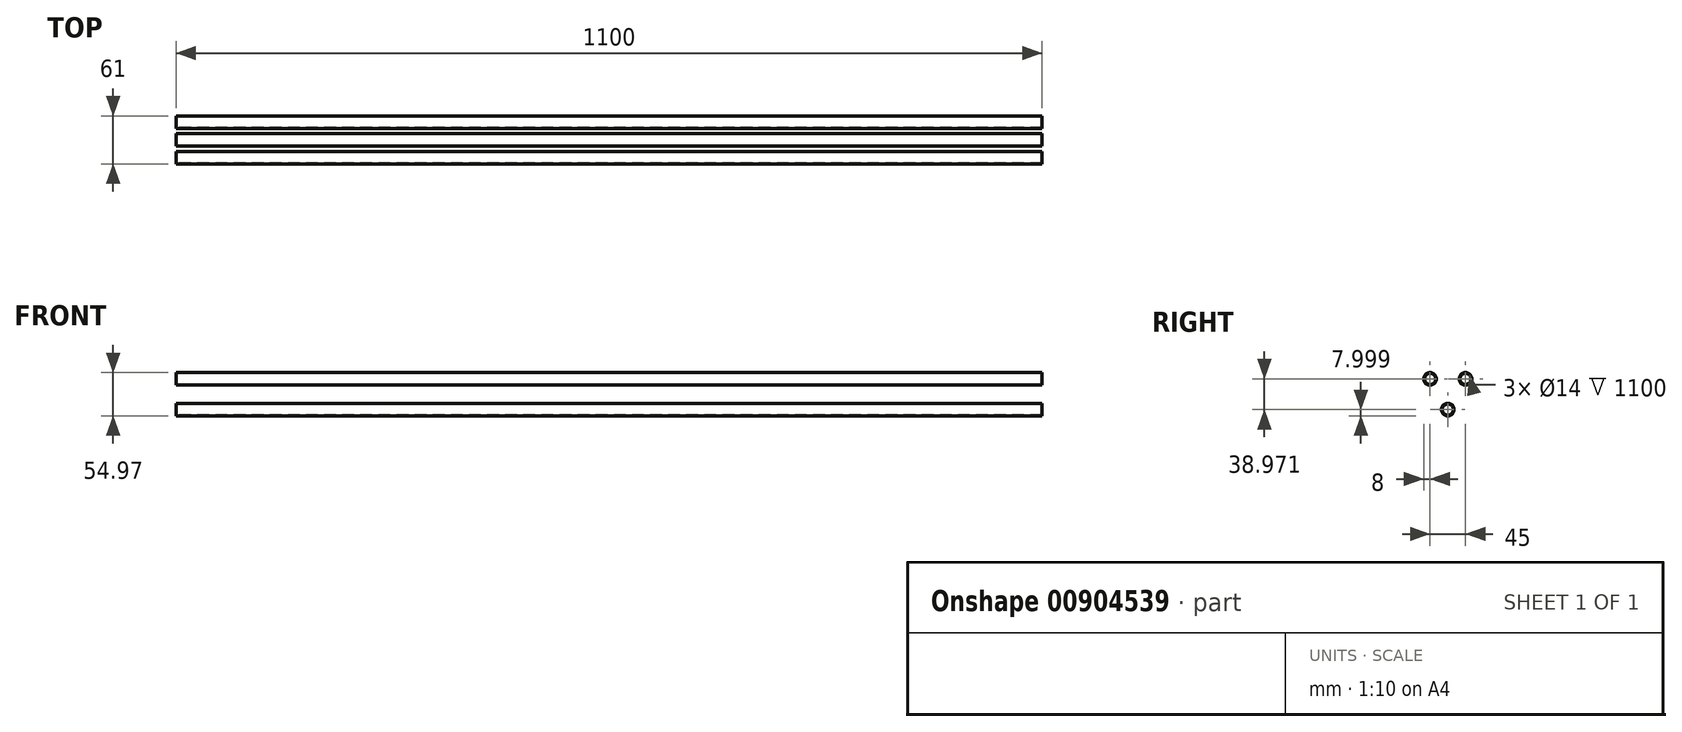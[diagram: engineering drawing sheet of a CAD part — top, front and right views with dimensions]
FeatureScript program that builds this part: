
annotation { "Feature Type Name" : "Feature", "Feature Type Description" : "" }
export const myFeature = defineFeature(function(context is Context, id is Id, definition is map)
    precondition{}
    {
        {
            var Q0;
            Q0=qCreatedBy(makeId("Right.planeOp"),FACE);
            var sketch = newSketch(context, id + "F0", { "sketchPlane" : qUnion([Q0])});
            skCircle(sketch, "E0", {"center": v(0, 0) * mm, "radius": 8 * mm});
            skCircle(sketch, "E1", {"center": v(45, 0) * mm, "radius": 8 * mm});
            skCircle(sketch, "E2", {"center": v(22.5, -38.97) * mm, "radius": 8 * mm});
            skCircle(sketch, "E3", {"center": v(0, 0) * mm, "radius": 7 * mm});
            skCircle(sketch, "E4", {"center": v(45, 0) * mm, "radius": 7 * mm});
            skCircle(sketch, "E5", {"center": v(22.5, -38.97) * mm, "radius": 7 * mm});
            skSolve(sketch);
        }
        {
            var Q0;
            Q0=makeQuery(id+"F0.imprint","IMPRINT",FACE,{"disambiguationData":[TD([[makeQuery(id+"F0.imprint","IMPRINT",EDGE,{"derivedFrom":sQuery(id+"F0.wireOp",EDGE,"E0")}),1.0]])]});
            var Q1;
            Q1=makeQuery(id+"F0.imprint","IMPRINT",FACE,{"disambiguationData":[TD([[makeQuery(id+"F0.imprint","IMPRINT",EDGE,{"derivedFrom":sQuery(id+"F0.wireOp",EDGE,"E1")}),1.0]])]});
            var Q2;
            Q2=makeQuery(id+"F0.imprint","IMPRINT",FACE,{"disambiguationData":[TD([[makeQuery(id+"F0.imprint","IMPRINT",EDGE,{"derivedFrom":sQuery(id+"F0.wireOp",EDGE,"E2")}),1.0]])]});
            extrude(context, id + "F1", {"entities" : qUnion([Q0, Q1, Q2]), "depth" : 1100 * mm, "offsetDistance" : 25 * mm});
        }
    });
